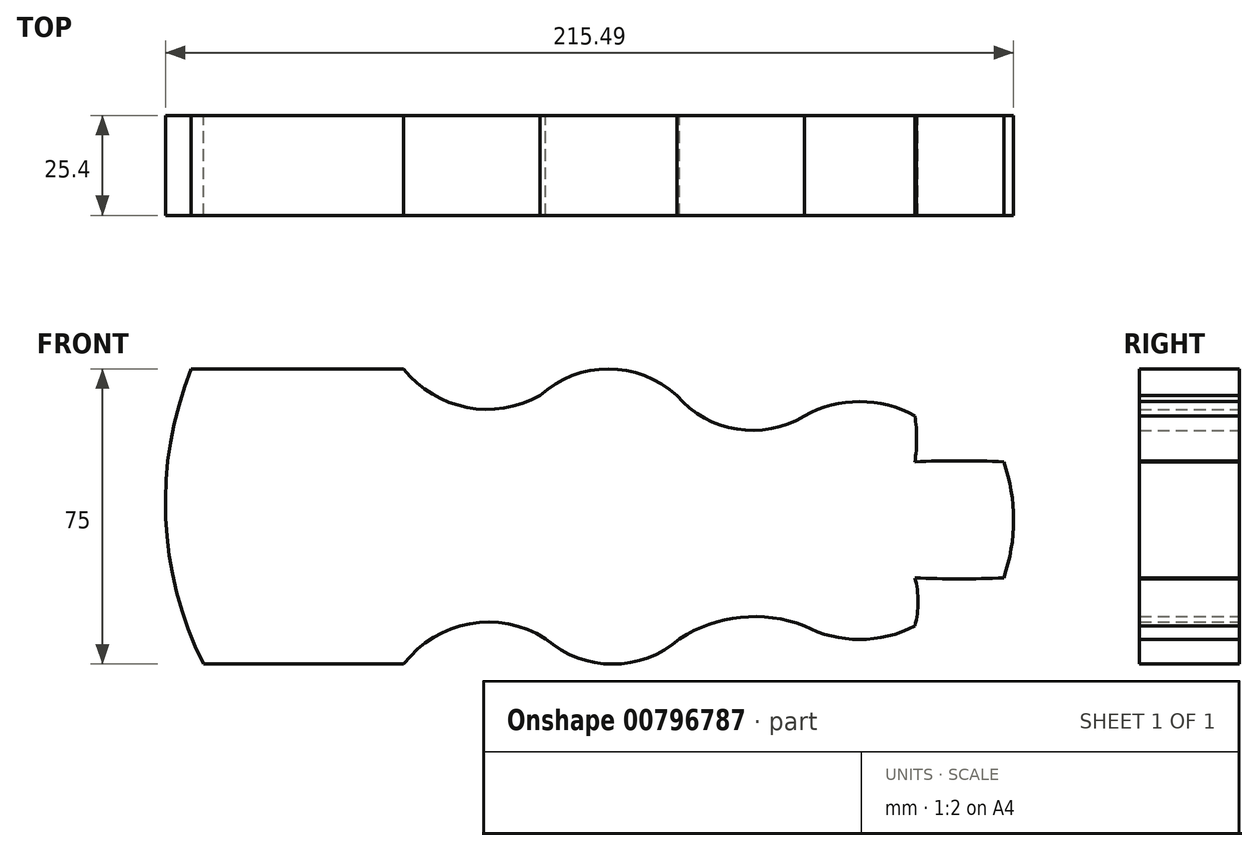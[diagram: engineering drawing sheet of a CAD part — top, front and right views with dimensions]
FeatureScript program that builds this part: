
annotation { "Feature Type Name" : "Feature", "Feature Type Description" : "" }
export const myFeature = defineFeature(function(context is Context, id is Id, definition is map)
    precondition{}
    {
        {
            var Q0;
            Q0=qCreatedBy(makeId("Front.planeOp"),FACE);
            var sketch = newSketch(context, id + "F0", { "sketchPlane" : qUnion([Q0])});
            skArc(sketch, "E0", {"start": v(69.39, 32.27) * mm, "mid": v(52, 39.03) * mm, "end": v(34.6, 32.27) * mm});
            skArc(sketch, "E1", {"start": v(36.04, -29.53) * mm, "mid": v(53.08, -35.97) * mm, "end": v(70.11, -29.53) * mm});
            skArc(sketch, "E2", {"start": v(34.6, 32.27) * mm, "mid": v(29.9, 1.24) * mm, "end": v(36.04, -29.53) * mm});
            skArc(sketch, "E3", {"start": v(69.39, 32.27) * mm, "mid": v(64.82, 1.31) * mm, "end": v(70.11, -29.53) * mm});
            skLineSegment(sketch, "E4", {"start": v(-53.97, 39.03) * mm, "end": v(0, 39.03) * mm});
            skPoint(sketch, "E4.startSnap0", {"position": v(52, 39.03) * mm});
            skLineSegment(sketch, "E5", {"start": v(0, -35.97) * mm, "end": v(-50.88, -35.97) * mm});
            skPoint(sketch, "E5.startSnap0", {"position": v(53.08, -35.97) * mm});
            skArc(sketch, "E6", {"start": v(-53.97, 39.03) * mm, "mid": v(-60.47, 1.2) * mm, "end": v(-50.88, -35.97) * mm});
            skArc(sketch, "E7", {"start": v(0, 39.03) * mm, "mid": v(16.05, 29.25) * mm, "end": v(34.6, 32.27) * mm});
            skArc(sketch, "E8", {"start": v(36.04, -29.53) * mm, "mid": v(16.77, -25.73) * mm, "end": v(0, -35.97) * mm});
            skArc(sketch, "E9", {"start": v(69.39, 32.27) * mm, "mid": v(84.64, 23.73) * mm, "end": v(101.8, 27.07) * mm});
            skArc(sketch, "E10", {"start": v(101.8, -26.27) * mm, "mid": v(85.56, -24.1) * mm, "end": v(70.11, -29.53) * mm});
            skArc(sketch, "E11", {"start": v(129.85, 27.07) * mm, "mid": v(115.82, 30.7) * mm, "end": v(101.8, 27.07) * mm});
            skArc(sketch, "E12", {"start": v(101.8, -26.27) * mm, "mid": v(115.82, -29.73) * mm, "end": v(129.85, -26.27) * mm});
            skArc(sketch, "E13", {"start": v(101.8, 27.07) * mm, "mid": v(98.1, 0.4) * mm, "end": v(101.8, -26.27) * mm});
            skArc(sketch, "E14", {"start": v(129.85, 15.4) * mm, "mid": v(130.32, 21.23) * mm, "end": v(129.85, 27.07) * mm});
            skArc(sketch, "E15", {"start": v(129.85, -26.27) * mm, "mid": v(130.65, -20.15) * mm, "end": v(129.85, -14.02) * mm});
            skArc(sketch, "E16", {"start": v(152.45, 15.4) * mm, "mid": v(141.15, 15.69) * mm, "end": v(129.85, 15.4) * mm});
            skArc(sketch, "E17", {"start": v(129.85, -14.02) * mm, "mid": v(141.15, -14.34) * mm, "end": v(152.45, -14.02) * mm});
            skArc(sketch, "E18", {"start": v(152.45, -14.02) * mm, "mid": v(154.95, 0.69) * mm, "end": v(152.45, 15.4) * mm});
            skArc(sketch, "E19", {"start": v(129.85, 15.4) * mm, "mid": v(128.09, 0.69) * mm, "end": v(129.85, -14.02) * mm});
            skSolve(sketch);
        }
        {
            var Q0;
            Q0 = qSketchRegion(id + "F0", true);
            extrude(context, id + "F1", {"entities" : qUnion([Q0]), "depth" : 25.4 * mm, "offsetDistance" : 25.4 * mm});
        }
    });
